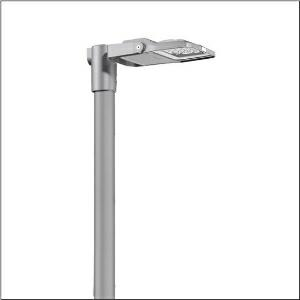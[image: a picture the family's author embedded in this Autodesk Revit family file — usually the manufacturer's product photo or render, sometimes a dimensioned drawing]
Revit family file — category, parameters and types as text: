
# Revit family: floodlight_fl_21_iq_micro___pl43_5xa7761a2a3a_2bb2
name_source: partatom
category: Lighting Fixtures
units: mm (PartAtom-declared; Revit-internal decimal feet)

## family parameters
Cut with Voids When Loaded = No
Host = Face
Light Source = No
Part Type = Normal
Room Calculation Point = No
Round Connector Dimension = Use Diameter
Shared = No

## types (1)
- --- (1 x LED, 3040 lm, 23.1 W, 3000K)
    Apparent Load = 23 VA
    CIE Flux Codes = 29 80 99 100 100
    Color Rendering = 70
    Color Temperature = 3000K
    Default Elevation = 1800 mm
    Description = Floodlight FL 21 iQ micro, floodlight, primary light control with lens, of PMMA, primary optical cover: protective disc, of toughened safety glass, transparent, light distribution: PL43, light emission: direct distribution, installation type: surface-mounted, lamps: LED, High Power LED, rated values: 3.040lm | 23,1W | 131,6lm/W (begin service life); end service life: 3.040lm | 23,8W; at 50% lumin. flux: 1.520lm | 11W | 138,2lm/W, colour temperature: 3000K, colour rendering: CRI > 70, light colour: 730, light setting 1 begin service life: 100% | 3.040lm | 23,1W | 131,6lm/W | 3.000K, light setting 1 end service life: 23,8W, further light settings possible, control: optimised constant luminous flux control (CLO 2.0), Desk-Remote (wireless, voltage-free reading and setting of iQ features in the workshop via application-optimized NFC function/RFID function), Light-Fading, Smart-Wire, Night-Set, Lumen-Switch, Temp-Guard, Auto-Match, pre-setting: linear dimming characteristic, with terminal, 6-pole, mains connection: 220..240V, AC, 50/60Hz, luminaire housing, of diecast aluminium, powder-coated, SITECO metallic grey (DB 702S), corrosivity category C5 mid according to DIN EN ISO 12944suitable for swimming poolschlorine-resistant, sealing non-destructively replaceable, please order mast flange separately, mast bracket, of steel, galvanised, powder-coated, SITECO metallic grey (DB 702S), protection rating (complete): IP66, insulation class (complete): insulation class II (safety insulation), certification: CE, ENEC, VDE, protection symbol: D, impact resistance: IK07, permissible operating ambient temperature: -40..+40°C, permissible operating ambient temperature for outdoor applications: -40..+50°C, standard: DIN EN 12944, LABS conformity tested according to VDMA 24364:2018-05, packaging unit: 1 piece

Light Distribution: PL43
    Height = 65 mm
    Lamp = 1 x LED
    Lamp Light Flux = 3040 lm
    Lamp Power = 23.1 W
    Lamp count = 1
    Length = 312 mm
    Luminous efficacy = 132 lm/W
    Manufacturer = Siteco
    ModVariant = No
    Model = 5XA7761A2A3A
    Number of Poles = 1
    OnlyDefault = Yes
    Power Factor = 1
    Product Name = Floodlight FL 21 iQ micro | PL43
    Product group = floodlight | pylon top
    ProductGroupID = 6101
    Protection Class = Protection class II
    Protection Degree = IP 66
    RLX_Detail_Level = 1
    RLX_Emergency_Light_Flux = 0 lm
    RLX_Emergency_Type = 0
    RLX_Emergency_Type_DB = No
    RlxData = <blob elided: 101805 chars, md5=6682b8ff>
    Socket = socket
    Standby Power = 0 W
    System Light Flux = 3040 lm
    System Power = 23 W
    Type Comments = factory setting: luminous flux: 100 % | dim-lin: 254 | 455 mA
    Type Image = l_1007121.jpg
    URL = http://relux.com
    VarID = @adj_176313
    Voltage = 0 V
    Weight = 0.00 kg
    Width = 230 mm

## geometry (parser evidence)
native form markers: Blend x4, Sweep x13
no freeform markers — native parametric forms only
